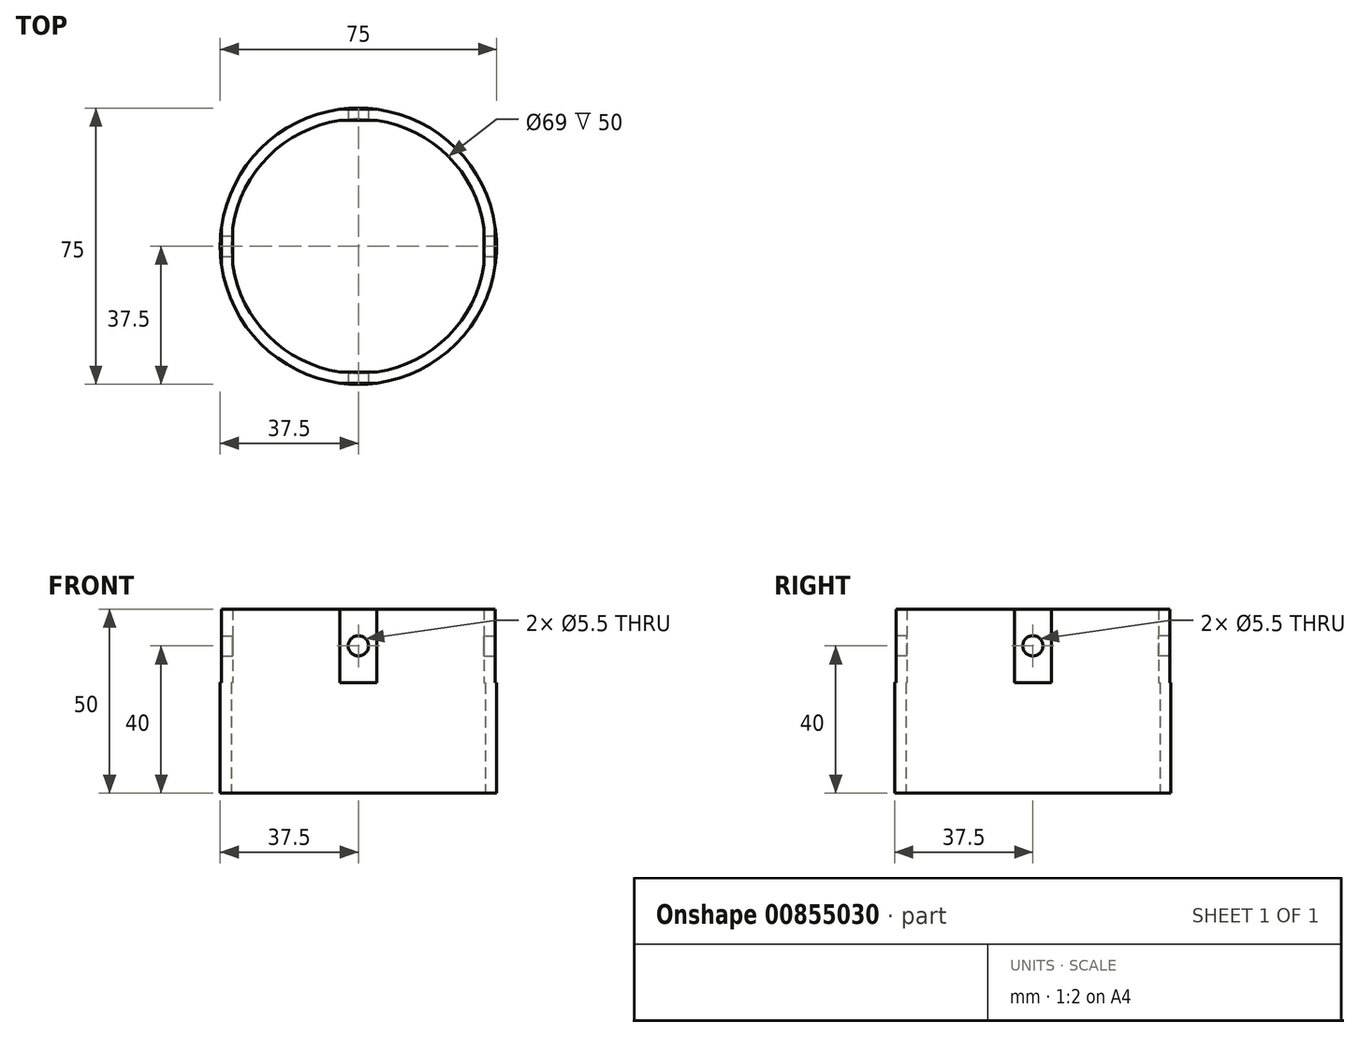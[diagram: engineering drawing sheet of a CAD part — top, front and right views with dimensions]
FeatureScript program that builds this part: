
annotation { "Feature Type Name" : "Feature", "Feature Type Description" : "" }
export const myFeature = defineFeature(function(context is Context, id is Id, definition is map)
    precondition{}
    {
        {
            var Q0;
            Q0=qCreatedBy(makeId("Top.planeOp"),FACE);
            var sketch = newSketch(context, id + "F0", { "sketchPlane" : qUnion([Q0])});
            skArc(sketch, "E0", {"start": v(37.17, 5) * mm, "mid": v(26.52, 26.52) * mm, "end": v(5, 37.17) * mm});
            skLineSegment(sketch, "E1.bottom", {"start": v(-5, 37.17) * mm, "end": v(5, 37.17) * mm});
            skLineSegment(sketch, "E1.top", {"start": v(-5, -37.17) * mm, "end": v(5, -37.17) * mm});
            skLineSegment(sketch, "E2.left", {"start": v(37.17, -5) * mm, "end": v(37.17, 5) * mm});
            skLineSegment(sketch, "E2.right", {"start": v(-37.17, -5) * mm, "end": v(-37.17, 5) * mm});
            skArc(sketch, "E3.trimOffspring", {"start": v(-5, 37.17) * mm, "mid": v(-26.52, 26.52) * mm, "end": v(-37.17, 5) * mm});
            skArc(sketch, "E4.trimOffspring", {"start": v(5, -37.17) * mm, "mid": v(26.52, -26.52) * mm, "end": v(37.17, -5) * mm});
            skArc(sketch, "E5.trimOffspring", {"start": v(-37.17, -5) * mm, "mid": v(-26.52, -26.52) * mm, "end": v(-5, -37.17) * mm});
            skArc(sketch, "E6", {"start": v(-34.14, -5) * mm, "mid": v(-24.4, -24.4) * mm, "end": v(-5, -34.14) * mm});
            skLineSegment(sketch, "E7.bottom", {"start": v(5, 34.14) * mm, "end": v(-5, 34.14) * mm});
            skLineSegment(sketch, "E7.top", {"start": v(5, -34.14) * mm, "end": v(-5, -34.14) * mm});
            skLineSegment(sketch, "E8.left", {"start": v(34.14, -5) * mm, "end": v(34.14, 5) * mm});
            skLineSegment(sketch, "E8.right", {"start": v(-34.14, -5) * mm, "end": v(-34.14, 5) * mm});
            skArc(sketch, "E9.trimOffspring", {"start": v(34.14, 5) * mm, "mid": v(24.4, 24.4) * mm, "end": v(5, 34.14) * mm});
            skArc(sketch, "E10.trimOffspring", {"start": v(-5, 34.14) * mm, "mid": v(-24.4, 24.4) * mm, "end": v(-34.14, 5) * mm});
            skArc(sketch, "E11.trimOffspring", {"start": v(5, -34.14) * mm, "mid": v(24.4, -24.4) * mm, "end": v(34.14, -5) * mm});
            skSolve(sketch);
        }
        {
            var Q0;
            Q0=makeQuery(id+"F0.imprint","IMPRINT",FACE,{"disambiguationData":[TD([[makeQuery(id+"F0.imprint","IMPRINT",EDGE,{"derivedFrom":sQuery(id+"F0.wireOp",EDGE,"E0")}),1.0]])]});
            extrude(context, id + "F1", {"entities" : qUnion([Q0]), "depth" : 20 * mm, "offsetDistance" : 25.4 * mm});
        }
        {
            var Q0;
            Q0=makeQuery(id+"F1.opExtrude","SWEPT_FACE",FACE,{"disambiguationData":[OSD([sQuery(id+"F0.wireOp",EDGE,"E2.left")])]});
            var sketch = newSketch(context, id + "F2", { "sketchPlane" : qUnion([Q0])});
            skPoint(sketch, "E12", {"position": v(0, 10) * mm});
            skPoint(sketch, "E12.positionSnap0", {"position": v(5, 10) * mm});
            skSolve(sketch);
        }
        {
            var Q0;
            Q0=sQuery(id+"F2.wireOp",VERTEX,"E12");
            var Q1;
            Q1=makeQuery(id+"F1.opExtrude","SWEPT_BODY",BODY,{"disambiguationData":[OSD([sQuery(id+"F0.wireOp",EDGE,"E0"),sQuery(id+"F0.wireOp",EDGE,"E1.bottom"),sQuery(id+"F0.wireOp",EDGE,"E1.top"),sQuery(id+"F0.wireOp",EDGE,"E2.left"),sQuery(id+"F0.wireOp",EDGE,"E2.right"),sQuery(id+"F0.wireOp",EDGE,"E3.trimOffspring"),sQuery(id+"F0.wireOp",EDGE,"E4.trimOffspring"),sQuery(id+"F0.wireOp",EDGE,"E5.trimOffspring"),sQuery(id+"F0.wireOp",EDGE,"E6"),sQuery(id+"F0.wireOp",EDGE,"E7.bottom"),sQuery(id+"F0.wireOp",EDGE,"E7.top"),sQuery(id+"F0.wireOp",EDGE,"E8.left"),sQuery(id+"F0.wireOp",EDGE,"E8.right"),sQuery(id+"F0.wireOp",EDGE,"E9.trimOffspring"),sQuery(id+"F0.wireOp",EDGE,"E10.trimOffspring"),sQuery(id+"F0.wireOp",EDGE,"E11.trimOffspring")])]});
            hole(context, id + "F3", {"style" : HoleStyle.SIMPLE, "endStyle" : HoleEndStyle.THROUGH, "holeDiameter" : 5.5 * mm, "majorDiameter" : 6.35 * mm, "isTappedThrough" : true, "tappedDepth" : 12.7 * mm, "tapClearance" : 3, "locations" : qUnion([Q0]), "scope" : qUnion([Q1])});
        }
        {
            var Q0;
            Q0=makeQuery(id+"F1.opExtrude","SWEPT_FACE",FACE,{"disambiguationData":[OSD([sQuery(id+"F0.wireOp",EDGE,"E1.top")])]});
            var sketch = newSketch(context, id + "F4", { "sketchPlane" : qUnion([Q0])});
            skPoint(sketch, "E13", {"position": v(0, 10) * mm});
            skPoint(sketch, "E13.positionSnap0", {"position": v(5, 10) * mm});
            skSolve(sketch);
        }
        {
            var Q0;
            Q0=sQuery(id+"F4.wireOp",VERTEX,"E13");
            var Q1;
            Q1=makeQuery(id+"F1.opExtrude","SWEPT_BODY",BODY,{"disambiguationData":[OSD([sQuery(id+"F0.wireOp",EDGE,"E0"),sQuery(id+"F0.wireOp",EDGE,"E1.bottom"),sQuery(id+"F0.wireOp",EDGE,"E1.top"),sQuery(id+"F0.wireOp",EDGE,"E2.left"),sQuery(id+"F0.wireOp",EDGE,"E2.right"),sQuery(id+"F0.wireOp",EDGE,"E3.trimOffspring"),sQuery(id+"F0.wireOp",EDGE,"E4.trimOffspring"),sQuery(id+"F0.wireOp",EDGE,"E5.trimOffspring"),sQuery(id+"F0.wireOp",EDGE,"E6"),sQuery(id+"F0.wireOp",EDGE,"E7.bottom"),sQuery(id+"F0.wireOp",EDGE,"E7.top"),sQuery(id+"F0.wireOp",EDGE,"E8.left"),sQuery(id+"F0.wireOp",EDGE,"E8.right"),sQuery(id+"F0.wireOp",EDGE,"E9.trimOffspring"),sQuery(id+"F0.wireOp",EDGE,"E10.trimOffspring"),sQuery(id+"F0.wireOp",EDGE,"E11.trimOffspring")])]});
            hole(context, id + "F5", {"style" : HoleStyle.SIMPLE, "endStyle" : HoleEndStyle.THROUGH, "holeDiameter" : 5.5 * mm, "majorDiameter" : 6.35 * mm, "isTappedThrough" : true, "tappedDepth" : 12.7 * mm, "tapClearance" : 3, "locations" : qUnion([Q0]), "scope" : qUnion([Q1])});
        }
        {
            var Q0;
            Q0=makeQuery(id+"F1.opExtrude","CAP_FACE",FACE,{"disambiguationData":[OSD([sQuery(id+"F0.wireOp",EDGE,"E0"),sQuery(id+"F0.wireOp",EDGE,"E1.bottom"),sQuery(id+"F0.wireOp",EDGE,"E1.top"),sQuery(id+"F0.wireOp",EDGE,"E2.left"),sQuery(id+"F0.wireOp",EDGE,"E2.right"),sQuery(id+"F0.wireOp",EDGE,"E3.trimOffspring"),sQuery(id+"F0.wireOp",EDGE,"E4.trimOffspring"),sQuery(id+"F0.wireOp",EDGE,"E5.trimOffspring"),sQuery(id+"F0.wireOp",EDGE,"E6"),sQuery(id+"F0.wireOp",EDGE,"E7.bottom"),sQuery(id+"F0.wireOp",EDGE,"E7.top"),sQuery(id+"F0.wireOp",EDGE,"E8.left"),sQuery(id+"F0.wireOp",EDGE,"E8.right"),sQuery(id+"F0.wireOp",EDGE,"E9.trimOffspring"),sQuery(id+"F0.wireOp",EDGE,"E10.trimOffspring"),sQuery(id+"F0.wireOp",EDGE,"E11.trimOffspring")])],"isStart":true});
            var sketch = newSketch(context, id + "F6", { "sketchPlane" : qUnion([Q0])});
            skCircle(sketch, "E14", {"center": v(0, 0) * mm, "radius": 37.5 * mm});
            skCircle(sketch, "E15", {"center": v(0, 0) * mm, "radius": 34.5 * mm});
            skSolve(sketch);
        }
        {
            var Q0;
            {var subQ14=makeQuery(id+"F1.opExtrude","CAP_EDGE",EDGE,{"disambiguationData":[OSD([sQuery(id+"F0.wireOp",EDGE,"E1.bottom")])],"isStart":true});Q0=makeQuery(id+"F6.imprint","IMPRINT",FACE,{"disambiguationData":[TD([[makeQuery(id+"F6.imprint","IMPRINT",EDGE,{"derivedFrom":subQ14}),1.0]])]});}
            var Q1;
            {var subQ1=makeQuery(id+"F1.opExtrude","CAP_EDGE",EDGE,{"disambiguationData":[OSD([sQuery(id+"F0.wireOp",EDGE,"E1.top")])],"isStart":true});Q1=makeQuery(id+"F6.imprint","IMPRINT",FACE,{"disambiguationData":[TD([[makeQuery(id+"F6.imprint","IMPRINT",EDGE,{"derivedFrom":subQ1}),1.0]])]});}
            var Q2;
            {var subQ1=makeQuery(id+"F1.opExtrude","CAP_EDGE",EDGE,{"disambiguationData":[OSD([sQuery(id+"F0.wireOp",EDGE,"E2.left")])],"isStart":true});Q2=makeQuery(id+"F6.imprint","IMPRINT",FACE,{"disambiguationData":[TD([[makeQuery(id+"F6.imprint","IMPRINT",EDGE,{"derivedFrom":subQ1}),1.0]])]});}
            var Q3;
            {var subQ1=makeQuery(id+"F1.opExtrude","CAP_EDGE",EDGE,{"disambiguationData":[OSD([sQuery(id+"F0.wireOp",EDGE,"E1.bottom")])],"isStart":true});Q3=makeQuery(id+"F6.imprint","IMPRINT",FACE,{"disambiguationData":[TD([[makeQuery(id+"F6.imprint","IMPRINT",EDGE,{"derivedFrom":subQ1}),-1.0]])]});}
            var Q4;
            {var subQ1=makeQuery(id+"F1.opExtrude","CAP_EDGE",EDGE,{"disambiguationData":[OSD([sQuery(id+"F0.wireOp",EDGE,"E2.right")])],"isStart":true});Q4=makeQuery(id+"F6.imprint","IMPRINT",FACE,{"disambiguationData":[TD([[makeQuery(id+"F6.imprint","IMPRINT",EDGE,{"derivedFrom":subQ1}),-1.0]])]});}
            extrude(context, id + "F7", {"entities" : qUnion([Q0, Q1, Q2, Q3, Q4]), "operationType" : NewBodyOperationType.ADD, "depth" : 30 * mm, "offsetDistance" : 25.4 * mm});
        }
    });
